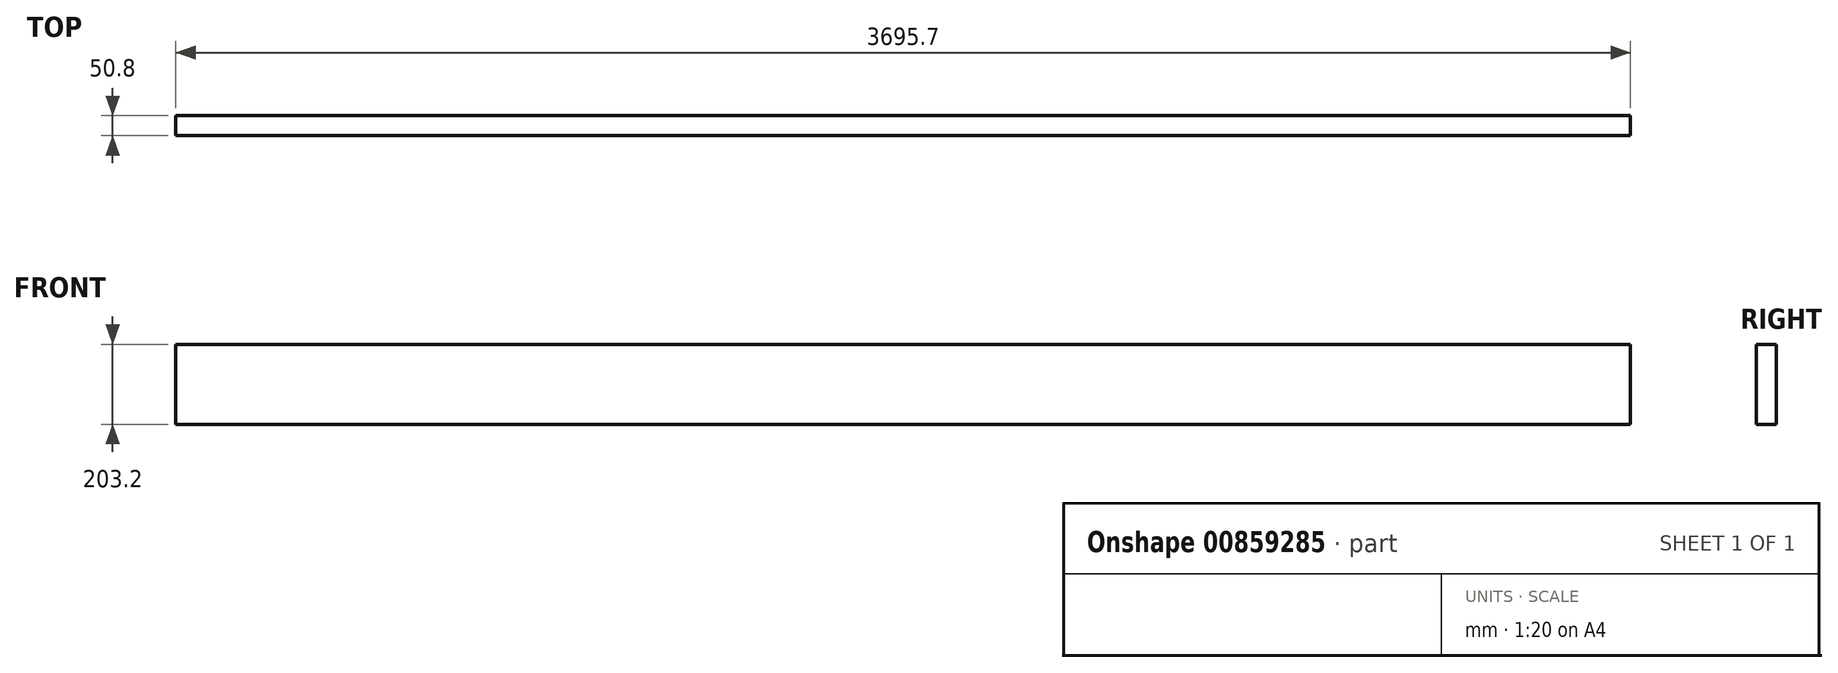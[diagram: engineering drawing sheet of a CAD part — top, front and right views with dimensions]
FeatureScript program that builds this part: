
annotation { "Feature Type Name" : "Feature", "Feature Type Description" : "" }
export const myFeature = defineFeature(function(context is Context, id is Id, definition is map)
    precondition{}
    {
        {
            var Q0;
            Q0=qCreatedBy(makeId("Right.planeOp"),FACE);
            var sketch = newSketch(context, id + "F0", { "sketchPlane" : qUnion([Q0])});
            skLineSegment(sketch, "E0.bottom", {"start": v(0, 0) * mm, "end": v(50.8, 0) * mm});
            skLineSegment(sketch, "E0.top", {"start": v(0, 203.2) * mm, "end": v(50.8, 203.2) * mm});
            skLineSegment(sketch, "E0.left", {"start": v(0, 0) * mm, "end": v(0, 203.2) * mm});
            skLineSegment(sketch, "E0.right", {"start": v(50.8, 0) * mm, "end": v(50.8, 203.2) * mm});
            skSolve(sketch);
        }
        {
            var Q0;
            Q0=makeQuery(id+"F0.imprint","IMPRINT",FACE,{"disambiguationData":[TD([[makeQuery(id+"F0.imprint","IMPRINT",EDGE,{"derivedFrom":sQuery(id+"F0.wireOp",EDGE,"E0.bottom")}),1.0]])]});
            extrude(context, id + "F1", {"entities" : qUnion([Q0]), "depth" : 3695.7 * mm, "offsetDistance" : 25 * mm});
        }
    });
